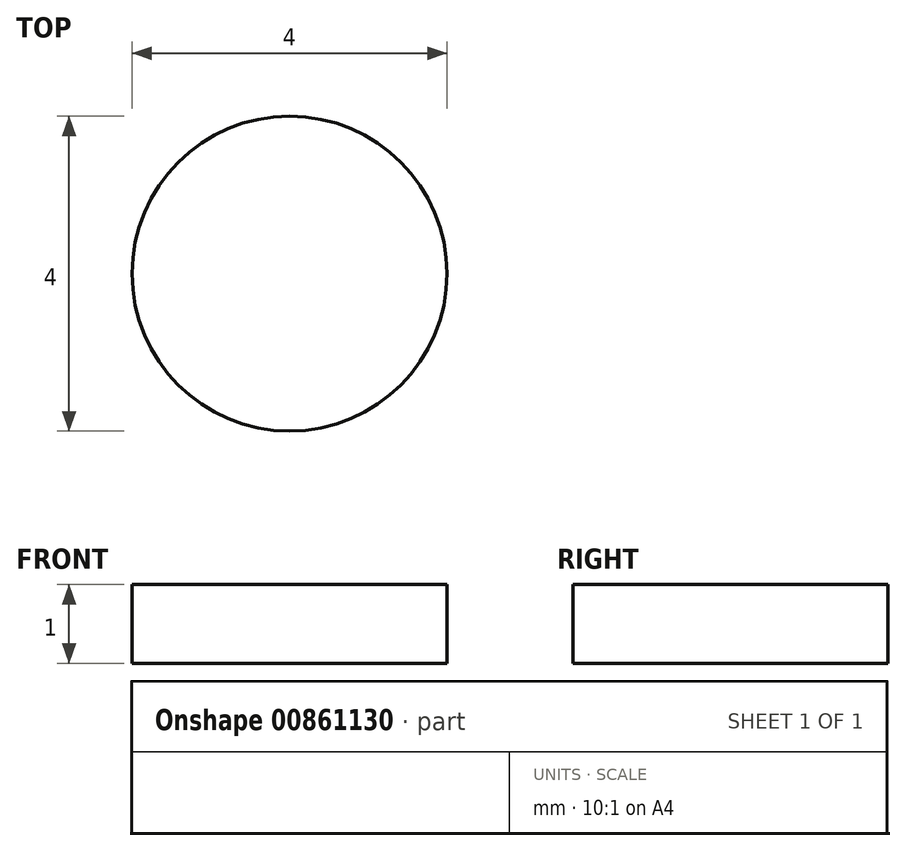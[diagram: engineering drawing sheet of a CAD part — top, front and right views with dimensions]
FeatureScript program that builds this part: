
annotation { "Feature Type Name" : "Feature", "Feature Type Description" : "" }
export const myFeature = defineFeature(function(context is Context, id is Id, definition is map)
    precondition{}
    {
        {
            var Q0;
            Q0=qCreatedBy(makeId("Top.planeOp"),FACE);
            var sketch = newSketch(context, id + "F0", { "sketchPlane" : qUnion([Q0])});
            skCircle(sketch, "E0", {"center": v(0, 0) * mm, "radius": 2 * mm});
            skSolve(sketch);
        }
        {
            var Q0;
            Q0=makeQuery(id+"F0.imprint","IMPRINT",FACE,{"disambiguationData":[TD([[makeQuery(id+"F0.imprint","IMPRINT",EDGE,{"derivedFrom":sQuery(id+"F0.wireOp",EDGE,"E0")}),1.0]])]});
            extrude(context, id + "F1", {"entities" : qUnion([Q0]), "depth" : 1 * mm, "offsetDistance" : 25 * mm});
        }
    });
